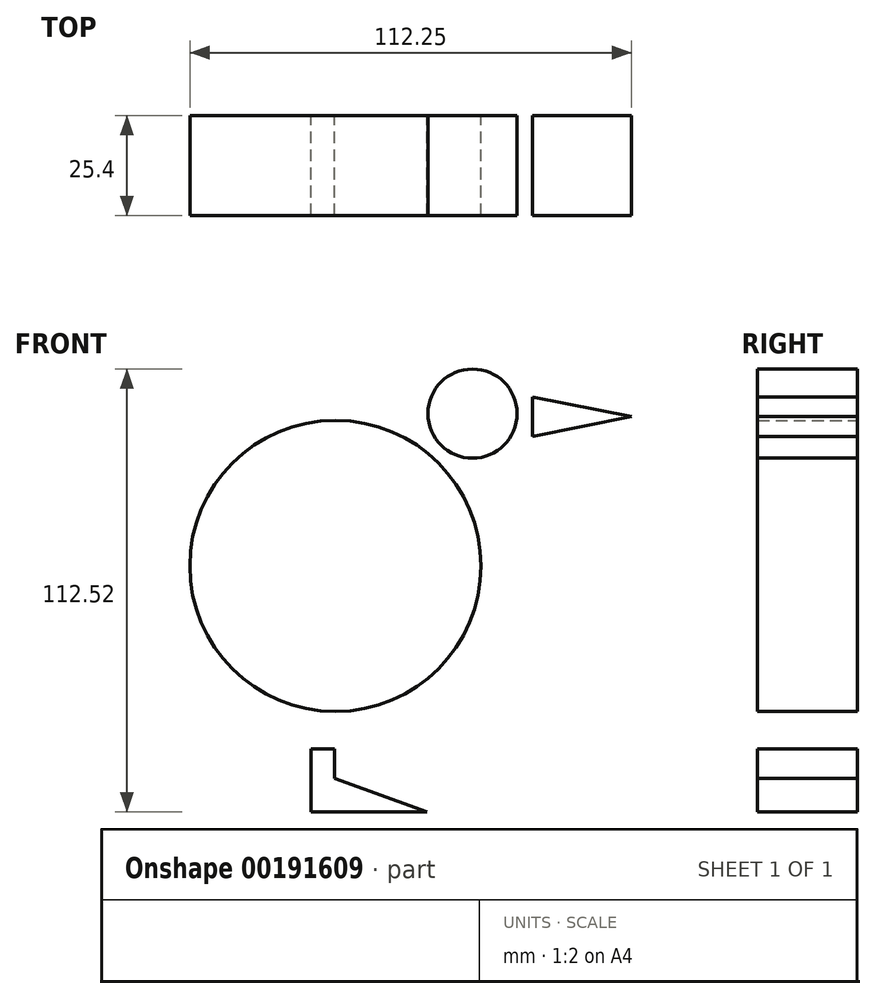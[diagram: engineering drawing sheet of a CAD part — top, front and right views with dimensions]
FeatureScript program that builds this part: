
annotation { "Feature Type Name" : "Feature", "Feature Type Description" : "" }
export const myFeature = defineFeature(function(context is Context, id is Id, definition is map)
    precondition{}
    {
        {
            var Q0;
            Q0=qCreatedBy(makeId("Front.planeOp"),FACE);
            var sketch = newSketch(context, id + "F0", { "sketchPlane" : qUnion([Q0])});
            skCircle(sketch, "E0", {"center": v(-23.32, -4.74) * mm, "radius": 36.98 * mm});
            skCircle(sketch, "E1", {"center": v(11.51, 33.96) * mm, "radius": 11.32 * mm});
            skLineSegment(sketch, "E2.left", {"start": v(26.8, 38.22) * mm, "end": v(26.8, 28.15) * mm});
            skLineSegment(sketch, "E3.bottom", {"start": v(-29.5, -51.18) * mm, "end": v(-23.5, -51.18) * mm});
            skLineSegment(sketch, "E3.top", {"start": v(-29.5, -67.24) * mm, "end": v(-23.5, -67.24) * mm});
            skLineSegment(sketch, "E3.left", {"start": v(-29.5, -51.18) * mm, "end": v(-29.5, -67.24) * mm});
            skLineSegment(sketch, "E3.right", {"start": v(-23.5, -51.18) * mm, "end": v(-23.5, -58.73) * mm});
            skLineSegment(sketch, "E4", {"start": v(-23.5, -67.24) * mm, "end": v(0, -67.24) * mm});
            skLineSegment(sketch, "E5", {"start": v(51.95, 33.18) * mm, "end": v(26.8, 38.22) * mm});
            skLineSegment(sketch, "E6", {"start": v(51.95, 33.18) * mm, "end": v(26.8, 28.15) * mm});
            skPoint(sketch, "E7.orphan", {"position": v(51.95, 28.15) * mm});
            skPoint(sketch, "E2.bottom.end.orphan", {"position": v(51.95, 38.22) * mm});
            skLineSegment(sketch, "E8", {"start": v(0, -67.24) * mm, "end": v(-23.5, -58.73) * mm});
            skSolve(sketch);
        }
        {
            var Q0;
            Q0 = qSketchRegion(id + "F0", true);
            extrude(context, id + "F1", {"entities" : qUnion([Q0]), "depth" : 25.4 * mm});
        }
    });
